FCSTD DOCUMENT  (FreeCAD 0.17R11939 (Git))
Label: mtmf_sketch
License: All rights reserved
LicenseURL: http://en.wikipedia.org/wiki/All_rights_reserved
objects: Sketcher::SketchObject×1, PartDesign::Body×1
note: 2 computed .brp shape members not serialized (recipe doc carries the construction recipe); baked Part::Feature solids carry a one-line shape summary decoded from their .brp

FEATURE [Sketcher::SketchObject] Sketch
  MapMode = 5
  Support = -> [XY_Plane]
  sketch-geometry (50):
    g0: LineSegment StartX=-114.3 StartY=0 StartZ=0 EndX=114.3 EndY=0 EndZ=0
    g1: LineSegment StartX=114.3 StartY=0 StartZ=0 EndX=114.3 EndY=-165.1 EndZ=0
    g2: LineSegment StartX=114.3 StartY=-165.1 StartZ=0 EndX=-114.3 EndY=-165.1 EndZ=0
    g3: LineSegment StartX=-114.3 StartY=-165.1 StartZ=0 EndX=-114.3 EndY=0 EndZ=0
    g4: Circle CenterX=0 CenterY=330.2 CenterZ=0 NormalX=0 NormalY=0 NormalZ=1 Radius=101.6
    g5: LineSegment StartX=-827.587 StartY=84.8662 StartZ=0 EndX=-85.8398 EndY=384.552 EndZ=0
    g6: LineSegment StartX=-23.9923 StartY=231.473 StartZ=0 EndX=-765.739 EndY=-68.2118 EndZ=0
    g7: LineSegment StartX=-765.739 StartY=-68.2118 StartZ=0 EndX=-827.587 EndY=84.8662 EndZ=0
    g8: LineSegment StartX=-42.5359 StartY=223.981 StartZ=0 EndX=35.8503 EndY=29.9685 EndZ=0
    g9: LineSegment StartX=35.8503 StartY=29.9685 StartZ=0 EndX=-38.3244 EndY=0 EndZ=0
    g10: LineSegment StartX=-38.3244 StartY=0 StartZ=0 EndX=-116.711 EndY=194.013 EndZ=0
    g11: LineSegment [constr] StartX=0 StartY=330.2 StartZ=0 EndX=-796.663 EndY=8.3272 EndZ=0
    g12: LineSegment StartX=-101.6 StartY=177.8 StartZ=0 EndX=101.6 EndY=177.8 EndZ=0
    g13: LineSegment [constr] StartX=0 StartY=228.6 StartZ=0 EndX=0 EndY=177.8 EndZ=0
    g14: LineSegment StartX=-101.6 StartY=177.8 StartZ=0 EndX=-101.6 EndY=238.057 EndZ=0
    g15: ArcOfCircle CenterX=0 CenterY=330.2 CenterZ=0 NormalX=0 NormalY=0 NormalZ=1 Radius=137.16 StartAngle=5.54656 EndAngle=10.1614
    g16: LineSegment StartX=101.6 StartY=238.057 StartZ=0 EndX=101.6 EndY=177.8 EndZ=0
    g17: LineSegment StartX=30 StartY=495.3 StartZ=0 EndX=30 EndY=469.9 EndZ=0
    g18: LineSegment StartX=30 StartY=469.9 StartZ=0 EndX=-30 EndY=469.9 EndZ=0
    g19: LineSegment StartX=-30 StartY=469.9 StartZ=0 EndX=-30 EndY=495.3 EndZ=0
    g20: LineSegment StartX=-9.525 StartY=469.9 StartZ=0 EndX=-9.525 EndY=404.55 EndZ=0
    g21: LineSegment StartX=-9.525 StartY=404.55 StartZ=0 EndX=9.525 EndY=404.55 EndZ=0
    g22: LineSegment StartX=9.525 StartY=404.55 StartZ=0 EndX=9.525 EndY=469.9 EndZ=0
    g23: LineSegment StartX=9.525 StartY=404.55 StartZ=0 EndX=25.4 EndY=404.55 EndZ=0
    g24: LineSegment StartX=25.4 StartY=404.55 StartZ=0 EndX=25.4 EndY=353.75 EndZ=0
    g25: LineSegment StartX=25.4 StartY=353.75 StartZ=0 EndX=-25.4 EndY=353.75 EndZ=0
    g26: LineSegment StartX=-25.4 StartY=353.75 StartZ=0 EndX=-25.4 EndY=404.55 EndZ=0
    g27: LineSegment StartX=-25.4 StartY=404.55 StartZ=0 EndX=-9.525 EndY=404.55 EndZ=0
    g28: LineSegment [constr] StartX=101.6 StartY=330.2 StartZ=0 EndX=137.16 EndY=330.2 EndZ=0
    g29: LineSegment [constr] StartX=0 StartY=431.8 StartZ=0 EndX=0 EndY=469.9 EndZ=0
    g30: LineSegment StartX=-9.51501 StartY=353.75 StartZ=0 EndX=-473.107 EndY=166.447 EndZ=0
    g31: LineSegment StartX=-30 StartY=495.3 StartZ=0 EndX=-60 EndY=495.3 EndZ=0
    g32: LineSegment StartX=-60 StartY=495.3 StartZ=0 EndX=-60 EndY=695.3 EndZ=0
    g33: LineSegment StartX=-60 StartY=695.3 StartZ=0 EndX=60 EndY=695.3 EndZ=0
    g34: LineSegment StartX=60 StartY=695.3 StartZ=0 EndX=60 EndY=495.3 EndZ=0
    g35: LineSegment StartX=60 StartY=495.3 StartZ=0 EndX=30 EndY=495.3 EndZ=0
    g36: LineSegment StartX=-9.51501 StartY=353.75 StartZ=0 EndX=9.51501 EndY=306.65 EndZ=0
    g37: LineSegment StartX=9.51501 StartY=306.65 StartZ=0 EndX=-454.077 EndY=119.346 EndZ=0
    g38: LineSegment StartX=-473.107 StartY=166.447 StartZ=0 EndX=-454.077 EndY=119.346 EndZ=0
    g39: LineSegment [constr] StartX=-9.51501 StartY=353.75 StartZ=0 EndX=-9.51501 EndY=298.961 EndZ=0
    g40: LineSegment StartX=-114.3 StartY=-165.1 StartZ=0 EndX=-292.1 EndY=-165.1 EndZ=0
    g41: LineSegment StartX=-292.1 StartY=-165.1 StartZ=0 EndX=-292.1 EndY=-342.9 EndZ=0
    g42: LineSegment StartX=-292.1 StartY=-342.9 StartZ=0 EndX=38.1 EndY=-541.02 EndZ=0
    g43: LineSegment StartX=38.1 StartY=-541.02 StartZ=0 EndX=292.1 EndY=-541.02 EndZ=0
    g44: LineSegment StartX=114.3 StartY=-165.1 StartZ=0 EndX=292.1 EndY=-165.1 EndZ=0
    g45: LineSegment StartX=292.1 StartY=-700 StartZ=0 EndX=292.1 EndY=600 EndZ=0
    g46: LineSegment StartX=101.6 StartY=177.8 StartZ=0 EndX=114.3 EndY=177.8 EndZ=0
    g47: LineSegment StartX=114.3 StartY=177.8 StartZ=0 EndX=114.3 EndY=0 EndZ=0
    g48: LineSegment StartX=-114.3 StartY=0 StartZ=0 EndX=-114.3 EndY=177.8 EndZ=0
    g49: LineSegment StartX=-114.3 StartY=177.8 StartZ=0 EndX=-101.6 EndY=177.8 EndZ=0
  constraints (157):
    c: Coincident(g0,g1)
    c: Coincident(g1,g2)
    c: Coincident(g2,g3)
    c: Coincident(g3,g0)
    c: Horizontal(g0)
    c: Horizontal(g2)
    c: Vertical(g1)
    c: Vertical(g3)
    c: PointOnObject(g0,g-1)
    c: Symmetric(g0,g0,g-2)
    c: Distance(g1) = 165.1
    c: Distance(g0) = 228.6
    c: Radius(g4) = 101.6
    c: Coincident(g6,g7)
    c: Coincident(g7,g5)
    c: PointOnObject(g4,g-2)
    c: Perpendicular(g5,g7)
    c: Parallel(g5,g6)
    c: Distance(g7) = 165.1
    c: Distance(g5) = 800
    c: Coincident(g8,g9)
    c: Coincident(g9,g10)
    c: Coincident(g11,g4)
    c: PointOnObject(g11,g7)
    c: Parallel(g11,g5)
    c: Parallel(g10,g8)
    c: PointOnObject(g10,g6)
    c: PointOnObject(g8,g6)
    c: Perpendicular(g10,g9)
    c: Perpendicular(g11,g10)
    c: Distance(g9) = 80
    c: Horizontal(g12)
    c: Symmetric(g12,g12,g-2)
    c: Distance(g12) = 203.2
    c: PointOnObject(g13,g4)
    c: PointOnObject(g13,g12)
    c: Vertical(g13)
    c: PointOnObject(g13,g-2)
    c: Distance(g13) = 50.8
    c: PointOnObject(g9,g0)
    c: Coincident(g14,g12)
    c: Vertical(g14)
    c: Coincident(g15,g4)
    c: Coincident(g15,g14)
    c: Coincident(g16,g15)
    c: Coincident(g16,g12)
    c: Vertical(g16)
    c: DistanceY(g0,g12) = 177.8
    c: Coincident(g17,g18)
    c: Coincident(g18,g19)
    c: Horizontal(g18)
    c: Vertical(g17)
    c: Vertical(g19)
    c: Symmetric(g17,g19,g-2)
    c: Distance(g17) = 25.4
    c: DistanceY(g0,g17) = 469.9
    c: PointOnObject(g20,g18)
    c: Vertical(g20)
    c: Coincident(g21,g20)
    c: Horizontal(g21)
    c: Coincident(g22,g21)
    c: Vertical(g22)
    c: PointOnObject(g22,g18)
    c: Symmetric(g22,g20,g-2)
    c: Distance(g20,g22) = 19.05
    c: Coincident(g23,g21)
    c: Horizontal(g23)
    c: Coincident(g24,g23)
    c: Vertical(g24)
    c: Coincident(g25,g24)
    c: Horizontal(g25)
    c: Coincident(g26,g25)
    c: Vertical(g26)
    c: Coincident(g27,g26)
    c: Coincident(g27,g20)
    c: Horizontal(g27)
    c: Equal(g27,g23)
    c: Distance(g25) = 50.8
    c: Distance(g24) = 50.8
    c: Distance(g9,g11) = 291.8
    c: PointOnObject(g28,g4)
    c: PointOnObject(g28,g15)
    c: Horizontal(g28)
    c: Perpendicular(g4,g28)
    c: Distance(g28) = 35.56
    c: PointOnObject(g29,g4)
    c: PointOnObject(g29,g18)
    c: Vertical(g29)
    c: Perpendicular(g4,g29)
    c: Parallel(g11,g30)
    c: Distance(g30,g11) = 25.4
    c: Distance(g22) = 65.3495
    c: Coincident(g31,g19)
    c: Coincident(g32,g31)
    c: Vertical(g32)
    c: Coincident(g33,g32)
    c: Horizontal(g33)
    c: Coincident(g34,g33)
    c: Vertical(g34)
    c: Coincident(g35,g34)
    c: Coincident(g35,g17)
    c: Horizontal(g31)
    c: Horizontal(g35)
    c: Equal(g35,g31)
    c: Distance(g34) = 200
    c: Distance(g33) = 120
    c: Distance(g18) = 60
    c: DistanceY(g29,g19) = 63.5
    c: PointOnObject(g6,g4)
    c: PointOnObject(g5,g4)
    c: Angle(g11,g-2) = 1.18682
    c: Symmetric(g5,g6,g11)
    c: Coincident(g36,g30)
    c: Coincident(g37,g36)
    c: PointOnObject(g4,g36)
    c: Perpendicular(g36,g11)
    c: Coincident(g38,g30)
    c: Coincident(g38,g37)
    c: Perpendicular(g11,g38)
    c: Parallel(g11,g37)
    c: Distance(g30) = 500
    c: Distance(g8,g6) = 20
    c: Symmetric(g37,g30,g11)
    c: Coincident(g39,g30)
    c: PointOnObject(g39,g37)
    c: Vertical(g39)
    c: Distance(g39) = 54.7896
    c: PointOnObject(g30,g25)
    c: Coincident(g40,g2)
    c: Horizontal(g40)
    c: Coincident(g41,g40)
    c: Vertical(g41)
    c: Coincident(g42,g41)
    c: Coincident(g43,g42)
    c: Horizontal(g43)
    c: Coincident(g44,g1)
    c: Horizontal(g44)
    c: Vertical(g45)
    c: PointOnObject(g44,g45)
    c: Equal(g44,g40)
    c: Distance(g41) = 177.8
    c: Distance(g43) = 254
    c: Distance(g44,g43) = 375.92
    c: PointOnObject(g43,g45)
    c: DistanceY(g45) = 600
    c: DistanceY(g45) = -700
    c: Distance(g40,g44) = 584.2
    c: Coincident(g12,g46)
    c: Horizontal(g46)
    c: Coincident(g46,g47)
    c: Vertical(g47)
    c: Coincident(g48,g49)
    c: Coincident(g49,g12)
    c: Horizontal(g49)
    c: Vertical(g48)
    c: Coincident(g0,g47)
    c: Coincident(g0,g48)
FEATURE [PartDesign::Body] Body
  Group = -> [Sketch]
  Origin = -> Origin
